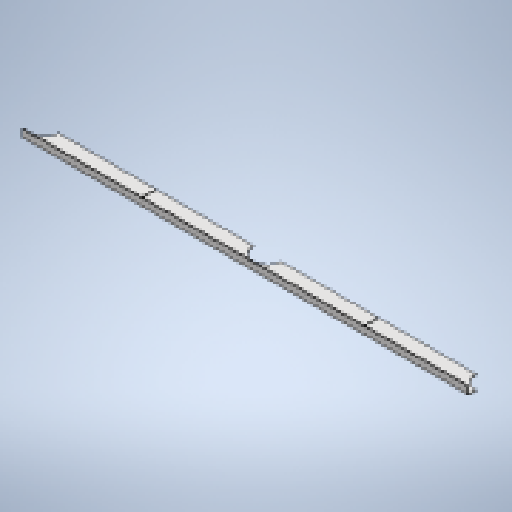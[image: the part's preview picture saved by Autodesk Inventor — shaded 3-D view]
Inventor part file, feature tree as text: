
AUTODESK INVENTOR PART (.ipt)
format: ipt  version: 2025 (Build 290162010, 162A)  size: 338,944 bytes
history: native  units: mm
features: other x5, sheet_metal_op x4, sketch x4, extrude x1
ambient origin geometry x8: Origin, YZ Plane, XZ Plane, XY Plane, X Axis, Y Axis, Z Axis, Center Point
bodies: Solid1 (feature_tree)
feature tree (14):
  sheet_metal_op  "Face1"
  sheet_metal_op  "Flange1"
  extrude  "Extrusion1"  Depth=50.0mm
  other  "Mark1"
  other  "A-Side Definition"
  sketch  "Sketch1"  dims[d0=980.0mm d1=50.0mm]
  other  "Plate1"
  sketch  "Sketch2"  dims[d2=2.0mm]
  other  "Plate2"
  sheet_metal_op  "Bend1"
  sheet_metal_op  "Corner1"
  sketch  "Sketch5"  dims[d3=2.0mm]
  sketch  "Sketch7"  dims[d4=1.0mm d5=4.0mm d6=2.75mm d7=20.0mm d8=90.0deg d9=2.75mm d10=8.0mm d11=2.0mm d12=2.75mm d15=0.0mm d16=0.0mm d30=12.0mm d33=60.0mm d34=2.0mm d35=31.0mm d36=490.0mm]
  other  "Definition1"
